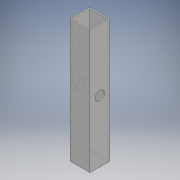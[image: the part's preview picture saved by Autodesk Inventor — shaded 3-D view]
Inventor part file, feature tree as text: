
AUTODESK INVENTOR PART (.ipt)
format: ipt  version: 2018 (Build 220112000, 112)  size: 105,472 bytes
history: native  units: mm
features: other x2, sketch x2, extrude x1, hole x1
ambient origin geometry x8: Origin, YZ Plane, XZ Plane, XY Plane, X Axis, Y Axis, Z Axis, Center Point
bodies: Body1 (feature_tree)
feature tree (6):
  other  "ソリッド1"
  extrude  "押し出し1"  Depth=32.0mm
  other  "作業平面1"
  hole  "穴1"  [1 undecoded]
  sketch  "スケッチ1"
  sketch  "スケッチ2"
note: 1 required parameter value undecoded (feature->parameter linkage not recoverable at this tier; creation-order binding heuristic only, values carry confidence <= 0.55)
